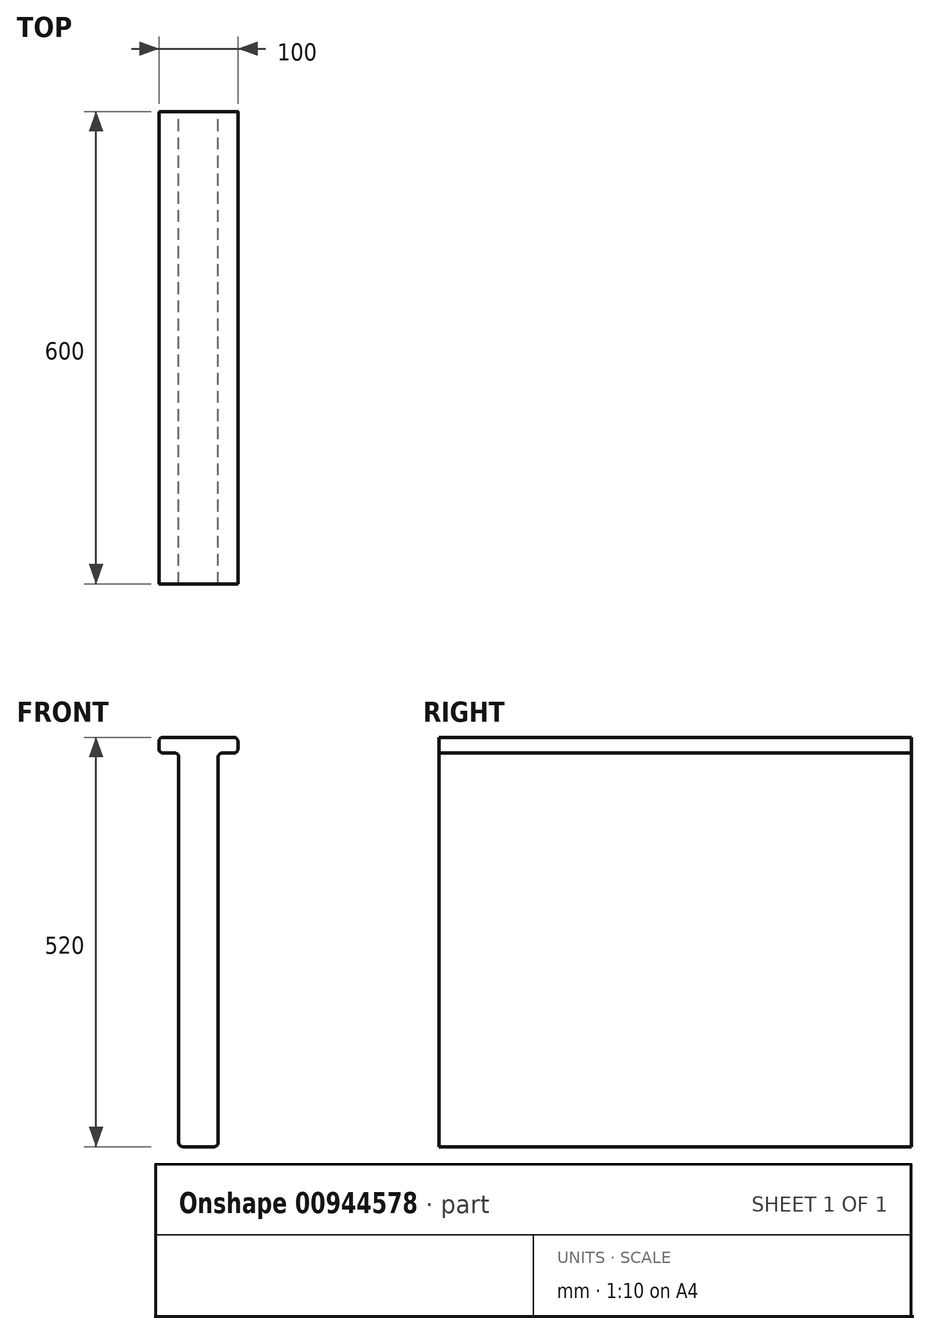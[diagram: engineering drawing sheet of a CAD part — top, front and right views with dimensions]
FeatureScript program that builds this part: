
annotation { "Feature Type Name" : "Feature", "Feature Type Description" : "" }
export const myFeature = defineFeature(function(context is Context, id is Id, definition is map)
    precondition{}
    {
        {
            var Q0;
            Q0=qCreatedBy(makeId("Front.planeOp"),FACE);
            var sketch = newSketch(context, id + "F0", { "sketchPlane" : qUnion([Q0])});
            skLineSegment(sketch, "E0", {"start": v(-5, 0) * mm, "end": v(-45, 0) * mm});
            skLineSegment(sketch, "E1", {"start": v(-50, 5) * mm, "end": v(-50, 495) * mm});
            skLineSegment(sketch, "E2", {"start": v(-55, 500) * mm, "end": v(-70, 500) * mm});
            skLineSegment(sketch, "E3", {"start": v(-75, 505) * mm, "end": v(-75, 515) * mm});
            skLineSegment(sketch, "E4", {"start": v(-70, 520) * mm, "end": v(20, 520) * mm});
            skLineSegment(sketch, "E5", {"start": v(25, 515) * mm, "end": v(25, 505) * mm});
            skLineSegment(sketch, "E6", {"start": v(20, 500) * mm, "end": v(5, 500) * mm});
            skLineSegment(sketch, "E7", {"start": v(0, 495) * mm, "end": v(0, 5) * mm});
            skPoint(sketch, "E8.visualSharp", {"position": v(-75, 520) * mm});
            skArc(sketch, "E8.filletArc", {"start": v(-70, 520) * mm, "mid": v(-73.54, 518.54) * mm, "end": v(-75, 515) * mm});
            skPoint(sketch, "E9.visualSharp", {"position": v(25, 520) * mm});
            skArc(sketch, "E9.filletArc", {"start": v(25, 515) * mm, "mid": v(23.54, 518.54) * mm, "end": v(20, 520) * mm});
            skPoint(sketch, "E10.visualSharp", {"position": v(25, 500) * mm});
            skArc(sketch, "E10.filletArc", {"start": v(20, 500) * mm, "mid": v(23.54, 501.46) * mm, "end": v(25, 505) * mm});
            skPoint(sketch, "E11.visualSharp", {"position": v(0, 500) * mm});
            skArc(sketch, "E11.filletArc", {"start": v(5, 500) * mm, "mid": v(1.46, 498.54) * mm, "end": v(0, 495) * mm});
            skPoint(sketch, "E12.visualSharp", {"position": v(-50, 500) * mm});
            skArc(sketch, "E12.filletArc", {"start": v(-50, 495) * mm, "mid": v(-51.46, 498.54) * mm, "end": v(-55, 500) * mm});
            skPoint(sketch, "E13.visualSharp", {"position": v(-75, 500) * mm});
            skArc(sketch, "E13.filletArc", {"start": v(-75, 505) * mm, "mid": v(-73.54, 501.46) * mm, "end": v(-70, 500) * mm});
            skPoint(sketch, "E14.visualSharp", {"position": v(-50, 0) * mm});
            skArc(sketch, "E14.filletArc", {"start": v(-50, 5) * mm, "mid": v(-48.54, 1.46) * mm, "end": v(-45, 0) * mm});
            skPoint(sketch, "E15.visualSharp", {"position": v(0, 0) * mm});
            skArc(sketch, "E15.filletArc", {"start": v(-5, 0) * mm, "mid": v(-1.46, 1.46) * mm, "end": v(0, 5) * mm});
            skSolve(sketch);
        }
        {
            var Q0;
            Q0=makeQuery(id+"F0.imprint","IMPRINT",FACE,{"disambiguationData":[TD([[makeQuery(id+"F0.imprint","IMPRINT",EDGE,{"derivedFrom":sQuery(id+"F0.wireOp",EDGE,"E0")}),-1.0]])]});
            extrude(context, id + "F1", {"entities" : qUnion([Q0]), "depth" : 600 * mm, "offsetDistance" : 25 * mm});
        }
    });
